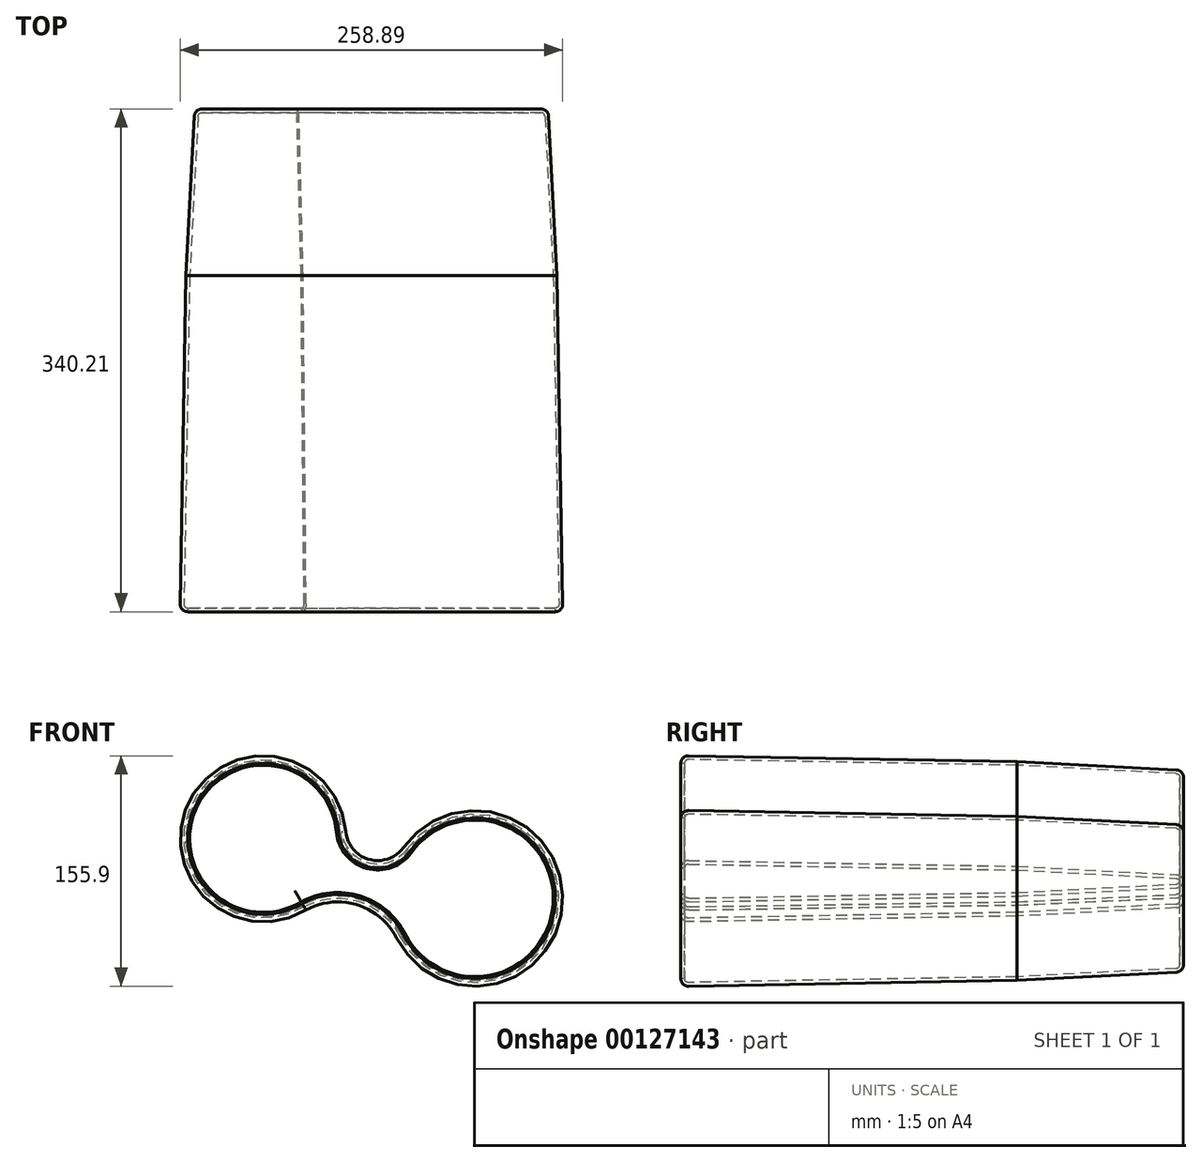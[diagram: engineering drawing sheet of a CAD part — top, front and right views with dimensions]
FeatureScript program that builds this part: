
annotation { "Feature Type Name" : "Feature", "Feature Type Description" : "" }
export const myFeature = defineFeature(function(context is Context, id is Id, definition is map)
    precondition{}
    {
        {
            var Q0;
            Q0=qCreatedBy(makeId("Front.planeOp"),FACE);
            var sketch = newSketch(context, id + "F0", { "sketchPlane" : qUnion([Q0])});
            skArc(sketch, "E0", {"start": v(17.82, 39.26) * mm, "mid": v(-80.89, 58.36) * mm, "end": v(-7.3, -10.15) * mm});
            skArc(sketch, "E1", {"start": v(17.82, 39.26) * mm, "mid": v(36.48, 16.93) * mm, "end": v(63.9, 26.67) * mm});
            skArc(sketch, "E2", {"start": v(63.9, 26.67) * mm, "mid": v(164.4, -9.89) * mm, "end": v(59.52, -30.8) * mm});
            skArc(sketch, "E3", {"start": v(59.52, -30.8) * mm, "mid": v(30.48, -6.31) * mm, "end": v(-7.3, -10.15) * mm});
            skSolve(sketch);
        }
        {
            var Q0;
            Q0=makeQuery(id+"F0.imprint","IMPRINT",FACE,{"disambiguationData":[TD([[makeQuery(id+"F0.imprint","IMPRINT",EDGE,{"derivedFrom":sQuery(id+"F0.wireOp",EDGE,"E0")}),1.0]])]});
            extrude(context, id + "F1", {"entities" : qUnion([Q0]), "depth" : 227.52 * mm, "hasDraft" : true, "draftAngle" : 1 * degree, "hasSecondDirection" : true, "secondDirectionOppositeDirection" : true, "secondDirectionDepth" : 112.7 * mm, "hasSecondDirectionDraft" : true, "secondDirectionDraftAngle" : 3 * degree, "secondDirectionDraftPullDirection" : true});
        }
        {
            var Q0;
            Q0=makeQuery(id+"F1.opExtrude","CAP_FACE",FACE,{"disambiguationData":[OSD([sQuery(id+"F0.wireOp",EDGE,"E0"),sQuery(id+"F0.wireOp",EDGE,"E1"),sQuery(id+"F0.wireOp",EDGE,"E2"),sQuery(id+"F0.wireOp",EDGE,"E3")])],"isStart":true});
            var Q1;
            Q1=makeQuery(id+"F1.opExtrude","CAP_EDGE",EDGE,{"disambiguationData":[OSD([sQuery(id+"F0.wireOp",EDGE,"E0")])],"isStart":true});
            var Q2;
            Q2=makeQuery(id+"F1.opExtrude","CAP_EDGE",EDGE,{"disambiguationData":[OSD([sQuery(id+"F0.wireOp",EDGE,"E0")])],"isStart":false});
            fillet(context, id + "F2", {"entities" : qUnion([Q0, Q1, Q2]), "radius" : 5.08 * mm, "tangentPropagation" : true, "allowEdgeOverflow" : false});
        }
        {
            var Q0;
            Q0=makeQuery(id+"F1.opExtrude","CAP_FACE",FACE,{"disambiguationData":[OSD([sQuery(id+"F0.wireOp",EDGE,"E0"),sQuery(id+"F0.wireOp",EDGE,"E1"),sQuery(id+"F0.wireOp",EDGE,"E2"),sQuery(id+"F0.wireOp",EDGE,"E3")])],"isStart":false});
            shell(context, id + "F3", {"entities" : qUnion([Q0]), "thickness" : 2.5 * mm});
        }
    });
